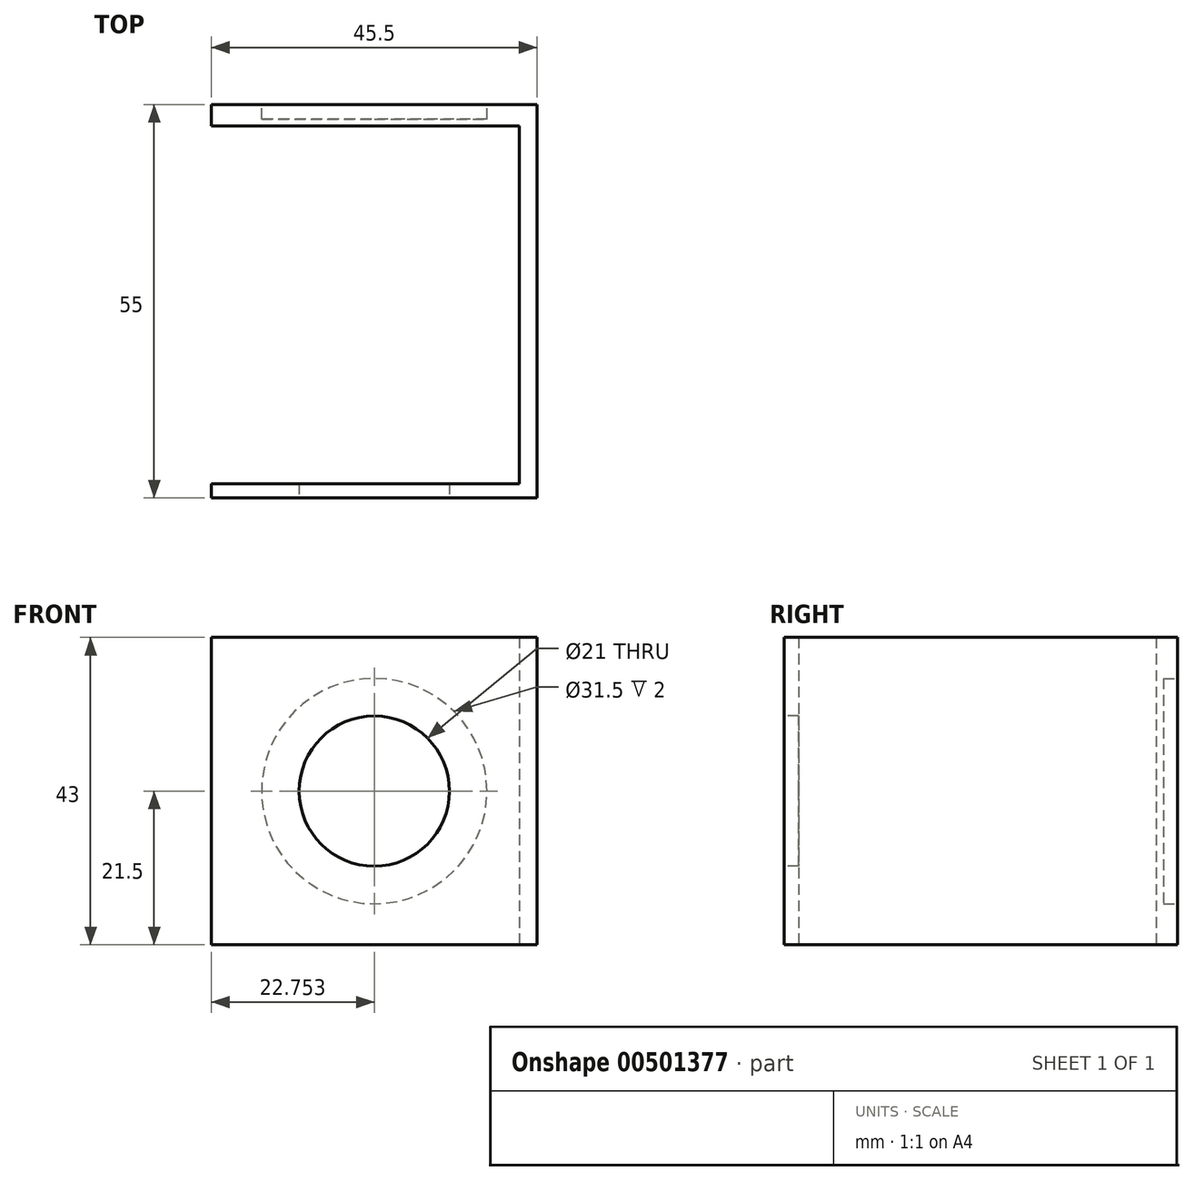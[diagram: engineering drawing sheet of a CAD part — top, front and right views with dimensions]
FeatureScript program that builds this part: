
annotation { "Feature Type Name" : "Feature", "Feature Type Description" : "" }
export const myFeature = defineFeature(function(context is Context, id is Id, definition is map)
    precondition{}
    {
        {
            var Q0;
            Q0=qCreatedBy(makeId("Top.planeOp"),FACE);
            var sketch = newSketch(context, id + "F0", { "sketchPlane" : qUnion([Q0])});
            skLineSegment(sketch, "E0", {"start": v(-15.14, 32.53) * mm, "end": v(30.36, 32.53) * mm});
            skLineSegment(sketch, "E1", {"start": v(30.36, 32.53) * mm, "end": v(30.36, -22.47) * mm});
            skLineSegment(sketch, "E2", {"start": v(30.36, -22.47) * mm, "end": v(-15.14, -22.47) * mm});
            skLineSegment(sketch, "E3", {"start": v(-15.14, -22.47) * mm, "end": v(-15.14, -20.47) * mm});
            skLineSegment(sketch, "E4", {"start": v(-15.14, -20.47) * mm, "end": v(27.86, -20.47) * mm});
            skLineSegment(sketch, "E5", {"start": v(27.86, -20.47) * mm, "end": v(27.86, 29.53) * mm});
            skLineSegment(sketch, "E6", {"start": v(27.86, 29.53) * mm, "end": v(-15.14, 29.53) * mm});
            skLineSegment(sketch, "E7", {"start": v(-15.14, 29.53) * mm, "end": v(-15.14, 32.53) * mm});
            skSolve(sketch);
        }
        {
            var Q0;
            Q0=makeQuery(id+"F0.imprint","IMPRINT",FACE,{"disambiguationData":[TD([[makeQuery(id+"F0.imprint","IMPRINT",EDGE,{"derivedFrom":sQuery(id+"F0.wireOp",EDGE,"E0")}),-1.0]])]});
            extrude(context, id + "F1", {"entities" : qUnion([Q0]), "depth" : 43 * mm});
        }
        {
            var Q0;
            Q0=makeQuery(id+"F1.opExtrude","SWEPT_FACE",FACE,{"disambiguationData":[OSD([sQuery(id+"F0.wireOp",EDGE,"E2")])]});
            var sketch = newSketch(context, id + "F2", { "sketchPlane" : qUnion([Q0])});
            skLineSegment(sketch, "E8", {"start": v(7.61, 43) * mm, "end": v(7.61, 0) * mm, "construction": true});
            skLineSegment(sketch, "E9", {"start": v(-15.14, 21.5) * mm, "end": v(30.36, 21.5) * mm, "construction": true});
            skCircle(sketch, "E10", {"center": v(7.61, 21.5) * mm, "radius": 10.5 * mm});
            skSolve(sketch);
        }
        {
            var Q0;
            Q0=makeQuery(id+"F2.imprint","IMPRINT",FACE,{"disambiguationData":[TD([[makeQuery(id+"F2.imprint","IMPRINT",EDGE,{"derivedFrom":sQuery(id+"F2.wireOp",EDGE,"E10")}),1.0]])]});
            var Q1;
            Q1=makeQuery(id+"F1.opExtrude","SWEPT_FACE",FACE,{"disambiguationData":[OSD([sQuery(id+"F0.wireOp",EDGE,"E4")])]});
            extrude(context, id + "F3", {"entities" : qUnion([Q0]), "operationType" : NewBodyOperationType.REMOVE, "endBound" : BoundingType.UP_TO_SURFACE, "oppositeDirection" : true, "endBoundEntityFace" : qUnion([Q1]), "depth" : 25 * mm});
        }
        {
            var Q0;
            Q0=makeQuery(id+"F1.opExtrude","SWEPT_FACE",FACE,{"disambiguationData":[OSD([sQuery(id+"F0.wireOp",EDGE,"E0")])]});
            var sketch = newSketch(context, id + "F4", { "sketchPlane" : qUnion([Q0])});
            skCircle(sketch, "E11", {"center": v(-7.61, 21.5) * mm, "radius": 15.75 * mm});
            skPoint(sketch, "E11.centerSnap0", {"position": v(15.14, 21.5) * mm});
            skPoint(sketch, "E11.centerSnap1", {"position": v(-7.61, 0) * mm});
            skSolve(sketch);
        }
        {
            var Q0;
            Q0=makeQuery(id+"F4.imprint","IMPRINT",FACE,{"disambiguationData":[TD([[makeQuery(id+"F4.imprint","IMPRINT",EDGE,{"derivedFrom":sQuery(id+"F4.wireOp",EDGE,"E11")}),1.0]])]});
            extrude(context, id + "F5", {"entities" : qUnion([Q0]), "operationType" : NewBodyOperationType.REMOVE, "oppositeDirection" : true, "depth" : 2 * mm, "offsetDistance" : 25 * mm});
        }
    });
